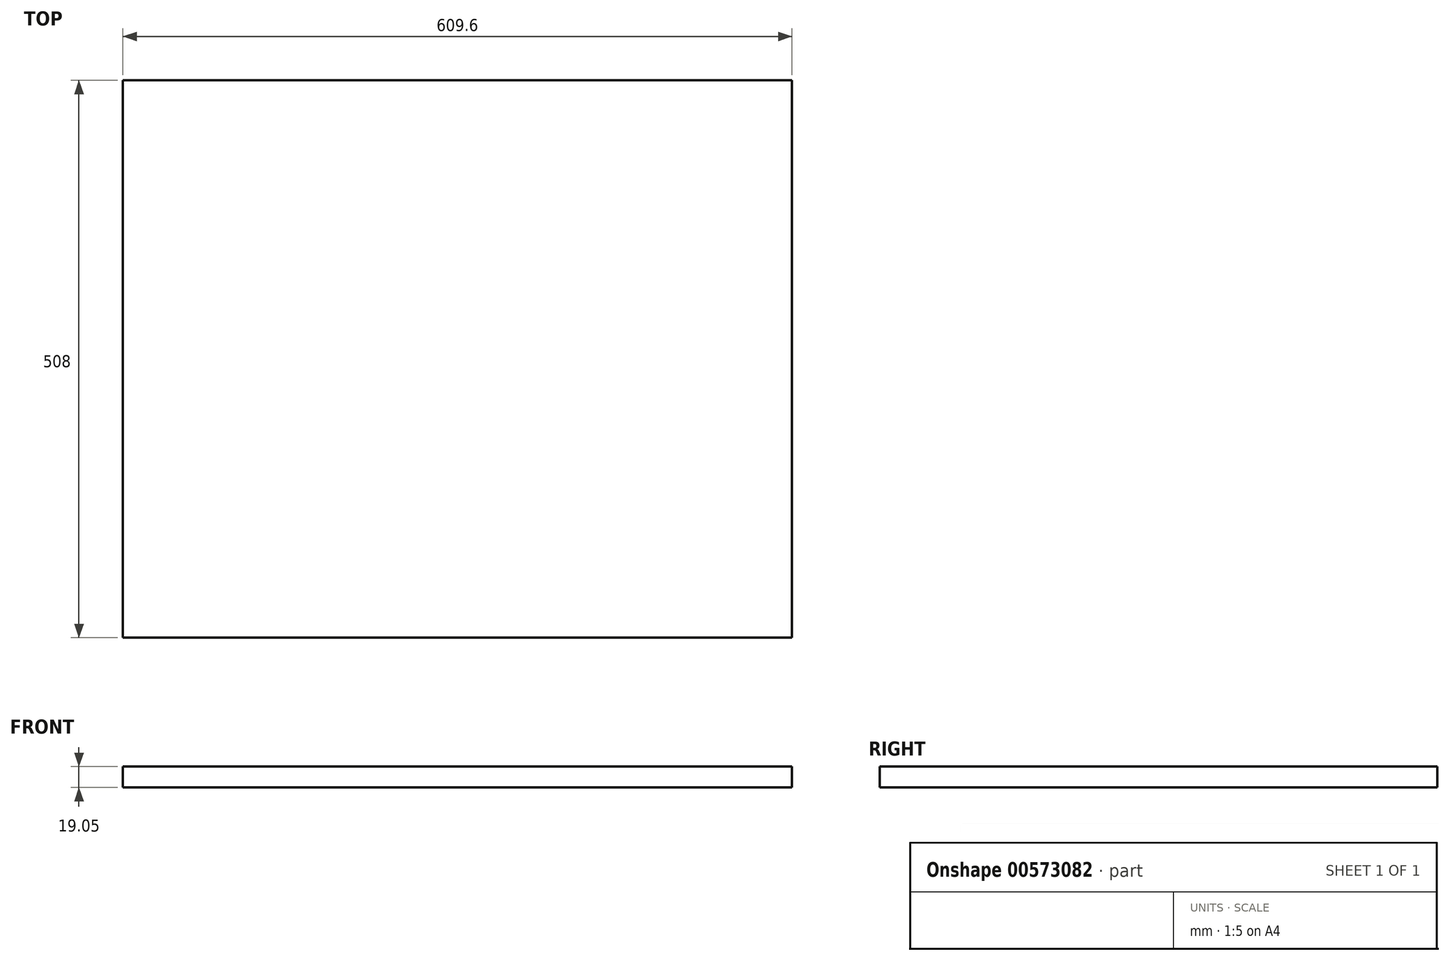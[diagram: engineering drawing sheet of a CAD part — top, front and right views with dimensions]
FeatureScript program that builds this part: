
annotation { "Feature Type Name" : "Feature", "Feature Type Description" : "" }
export const myFeature = defineFeature(function(context is Context, id is Id, definition is map)
    precondition{}
    {
        {
            var Q0;
            Q0=qCreatedBy(makeId("Top.planeOp"),FACE);
            var sketch = newSketch(context, id + "F0", { "sketchPlane" : qUnion([Q0])});
            skLineSegment(sketch, "E0.bottom", {"start": v(304.8, 254) * mm, "end": v(-304.8, 254) * mm});
            skLineSegment(sketch, "E0.top", {"start": v(304.8, -254) * mm, "end": v(-304.8, -254) * mm});
            skLineSegment(sketch, "E0.left", {"start": v(304.8, 254) * mm, "end": v(304.8, -254) * mm});
            skLineSegment(sketch, "E0.right", {"start": v(-304.8, 254) * mm, "end": v(-304.8, -254) * mm});
            skPoint(sketch, "E0.middle", {"position": v(0, 0) * mm});
            skSolve(sketch);
        }
        {
            var Q0;
            Q0=makeQuery(id+"F0.imprint","IMPRINT",FACE,{"disambiguationData":[TD([[makeQuery(id+"F0.imprint","IMPRINT",EDGE,{"derivedFrom":sQuery(id+"F0.wireOp",EDGE,"E0.bottom")}),1.0]])]});
            extrude(context, id + "F1", {"entities" : qUnion([Q0]), "depth" : 19.05 * mm, "offsetDistance" : 25.4 * mm});
        }
    });
